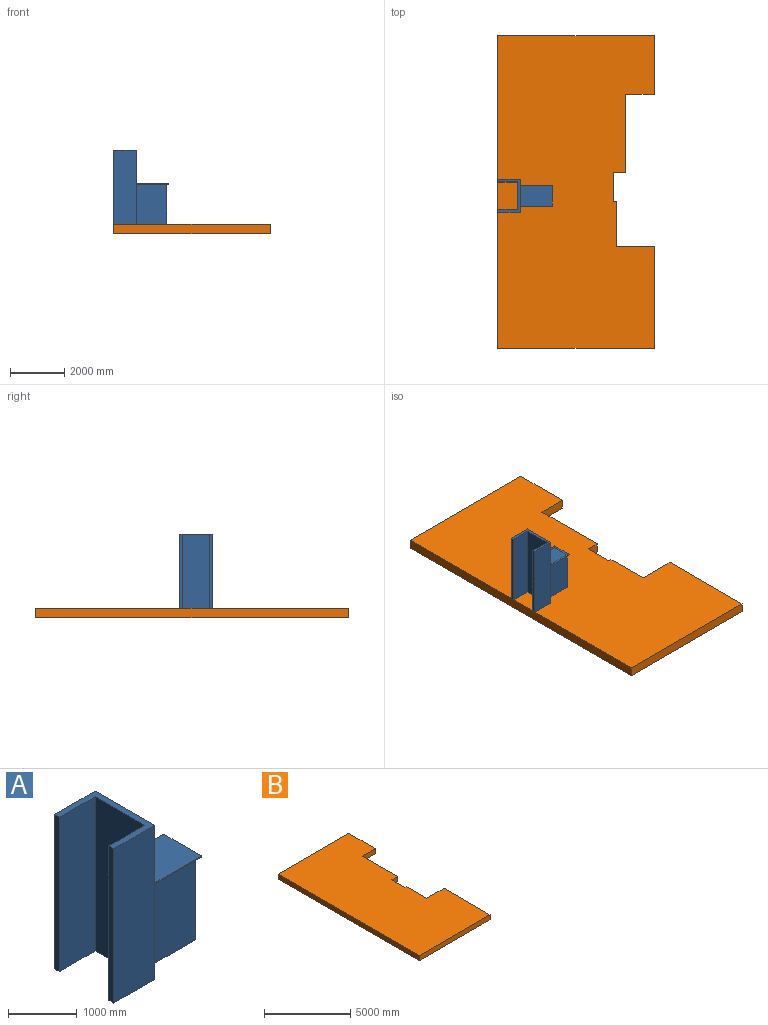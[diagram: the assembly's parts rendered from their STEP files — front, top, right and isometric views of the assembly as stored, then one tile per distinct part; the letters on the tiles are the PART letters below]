
ASSEMBLY  parts=2 mates=1
PART A: 18 faces, bbox 2025.7x1219.2x2743.2 mm
  f0: plane 2743.2x1219.2mm, normal (1,0,0), area 2375559.8mm2, adj f1,f7,f8,f9,f10,f11,f13,f14
  f1: plane 2743.2x838.2mm, normal (0,1,0), area 2299350.2mm2, adj f0,f2,f8,f9
  f2: plane 2743.2x101.6mm, normal (-1,0,0), area 278709.1mm2, adj f1,f3,f8,f9
  f3: plane 2743.2x736.6mm, normal (0,-1,0), area 2020641.1mm2, adj f2,f4,f8,f9
  f4: plane 2743.2x1016mm, normal (-1,0,0), area 2787091.2mm2, adj f3,f5,f8,f9
  f5: plane 2743.2x736.6mm, normal (0,1,0), area 2020641.1mm2, adj f4,f6,f8,f9
  f6: plane 2743.2x101.6mm, normal (-1,0,0), area 278709.1mm2, adj f5,f7,f8,f9
  f7: plane 2743.2x838.2mm, normal (0,-1,0), area 2299350.2mm2, adj f0,f6,f8,f9
  f8: plane 1219.2x838.2mm, normal (0,0,1), area 273547.8mm2, adj f0,f1,f2,f3,f4,f5,f6,f7
  f9: plane 1962.15x1219.2mm, normal (0,0,-1), area 1001530.3mm2, adj f0,f1,f2,f3,f4,f5,f6,f7
  f10: plane 1473.2x1123.95mm, normal (0,-1,0), area 1655803.1mm2, adj f0,f9,f12,f17
  f11: plane 1473.2x1123.95mm, normal (0,1,0), area 1655803.1mm2, adj f0,f9,f12,f17
  f12: plane 1473.2x647.7mm, normal (1,0,0), area 954191.6mm2, adj f9,f10,f11,f17
  f13: plane 1187.45x19.05mm, normal (0,1,0), area 22620.9mm2, adj f0,f15,f16,f17
  f14: plane 1187.45x19.05mm, normal (0,-1,0), area 22620.9mm2, adj f0,f15,f16,f17
  f15: plane 774.7x19.05mm, normal (1,0,0), area 14758mm2, adj f13,f14,f16,f17
  f16: plane 1187.45x774.7mm, normal (0,0,1), area 919917.5mm2, adj f0,f13,f14,f15
  f17: plane 1187.45x774.7mm, normal (0,0,-1), area 191935.1mm2, adj f0,f10,f11,f12,f13,f14,f15
PART B: 14 faces, bbox 5791.2x11557x355.6 mm
  f0: plane 11557x355.6mm, normal (-1,0,0), area 4109669.2mm2, adj f1,f11,f12,f13
  f1: plane 5791.2x355.6mm, normal (0,-1,0), area 2059350.7mm2, adj f0,f2,f12,f13
  f2: plane 3759.2x355.6mm, normal (1,0,0), area 1336771.5mm2, adj f1,f3,f12,f13
  f3: plane 1409.7x355.6mm, normal (0,1,0), area 501289.3mm2, adj f2,f4,f12,f13
  f4: plane 1676.4x355.6mm, normal (1,0,0), area 596127.8mm2, adj f3,f5,f12,f13
  f5: plane 355.6x114.3mm, normal (0,1,0), area 40645.1mm2, adj f4,f6,f12,f13
  f6: plane 1066.8x355.6mm, normal (1,0,0), area 379354.1mm2, adj f5,f7,f12,f13
  f7: plane 457.2x355.6mm, normal (0,-1,0), area 162580.3mm2, adj f6,f8,f12,f13
  f8: plane 2882.9x355.6mm, normal (1,0,0), area 1025159.2mm2, adj f7,f9,f12,f13
  f9: plane 1066.8x355.6mm, normal (0,-1,0), area 379354.1mm2, adj f8,f10,f12,f13
  f10: plane 2171.7x355.6mm, normal (1,0,0), area 772256.5mm2, adj f9,f11,f12,f13
  f11: plane 5791.2x355.6mm, normal (0,1,0), area 2059350.7mm2, adj f0,f10,f12,f13
  f12: plane 11557x5791.2mm, normal (0,0,1), area 59864396.4mm2, adj f0,f1,f2,f3,f4,f5,f6,f7
  f13: plane 11557x5791.2mm, normal (0,0,-1), area 59864396.4mm2, adj f0,f1,f2,f3,f4,f5,f6,f7
PLACE A t=(-787.13,-461.39,-1366.01)mm
PLACE B t=(1689.37,-321.69,-1721.61)mm
MATE fastened B.f12 <-> A.f9  axis (0,0,1) through (-1206.23,-1070.99,-1366.01)mm
